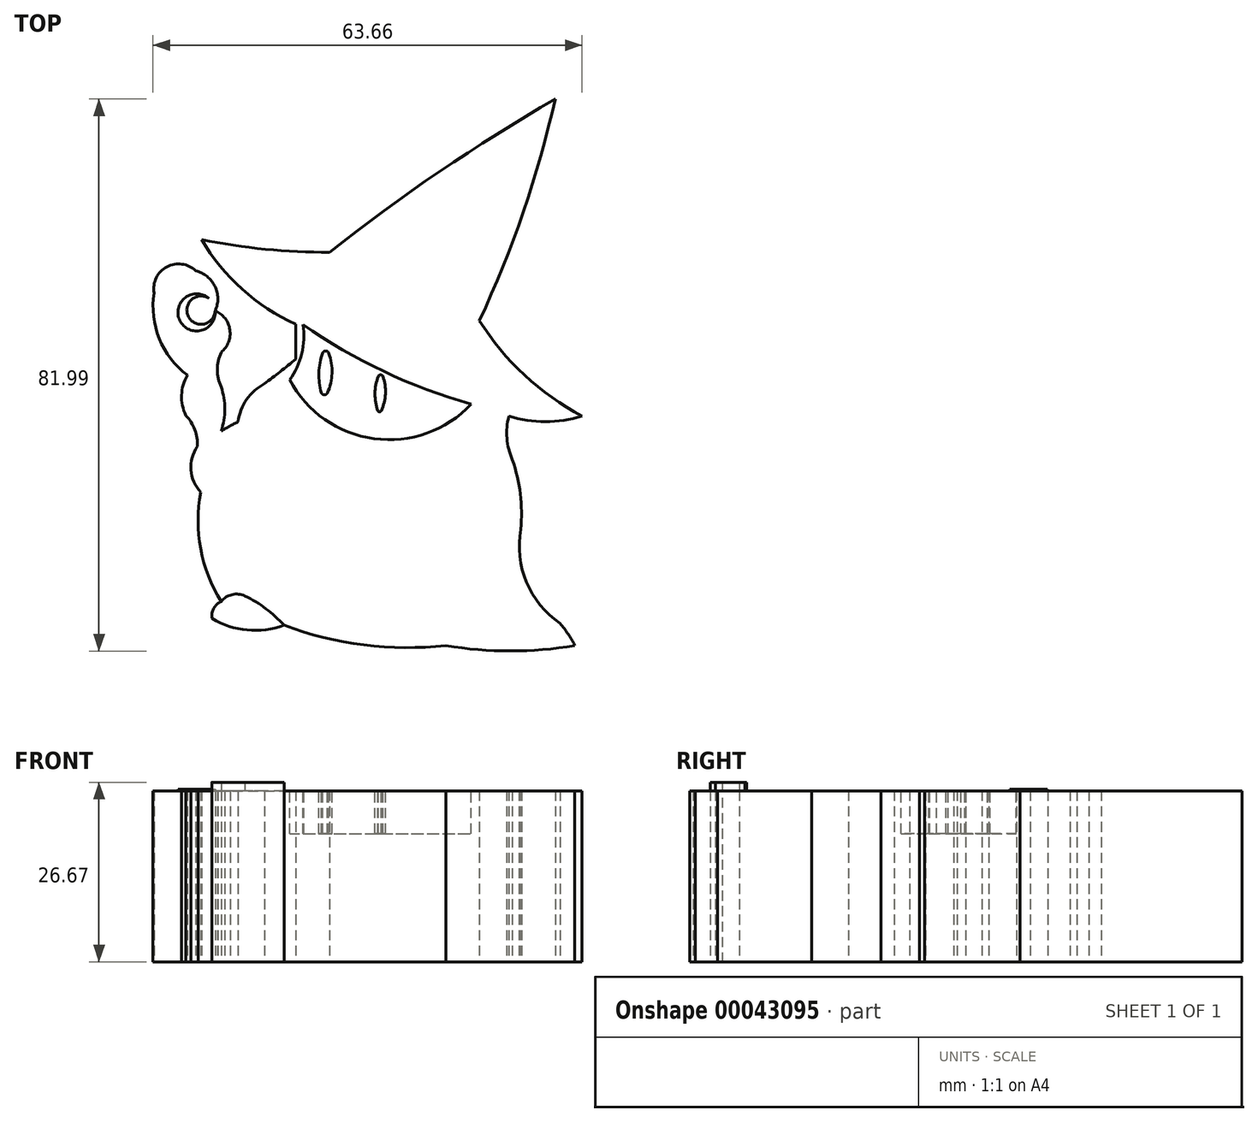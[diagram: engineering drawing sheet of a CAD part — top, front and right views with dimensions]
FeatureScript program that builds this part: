
annotation { "Feature Type Name" : "Feature", "Feature Type Description" : "" }
export const myFeature = defineFeature(function(context is Context, id is Id, definition is map)
    precondition{}
    {
        {
            var Q0;
            Q0=qCreatedBy(makeId("Top.planeOp"),FACE);
            var sketch = newSketch(context, id + "F0", { "sketchPlane" : qUnion([Q0])});
            skPoint(sketch, "E0", {"position": v(49.54, 7.17) * mm});
            skPoint(sketch, "E1", {"position": v(68.68, 7.17) * mm});
            skPoint(sketch, "E2", {"position": v(25.5, 10.19) * mm});
            skPoint(sketch, "E3", {"position": v(14.8, 11.2) * mm});
            skPoint(sketch, "E4", {"position": v(16.18, 13.71) * mm});
            skPoint(sketch, "E5", {"position": v(13.16, 29.95) * mm});
            skPoint(sketch, "E6", {"position": v(12.66, 36.75) * mm});
            skPoint(sketch, "E7", {"position": v(11.15, 47.32) * mm});
            skPoint(sketch, "E8", {"position": v(6.22, 59.55) * mm});
            skPoint(sketch, "E9", {"position": v(12.39, 62.82) * mm});
            skPoint(sketch, "E10", {"position": v(15.29, 56.9) * mm});
            skPoint(sketch, "E11", {"position": v(16.17, 50.73) * mm});
            skPoint(sketch, "E12", {"position": v(16.17, 45.57) * mm});
            skPoint(sketch, "E13", {"position": v(16.17, 39.03) * mm});
            skPoint(sketch, "E14", {"position": v(18.68, 40.41) * mm});
            skPoint(sketch, "E15", {"position": v(22.59, 46.08) * mm});
            skPoint(sketch, "E16", {"position": v(27.24, 49.73) * mm});
            skPoint(sketch, "E17", {"position": v(27.24, 54.89) * mm});
            skPoint(sketch, "E18", {"position": v(13.27, 67.48) * mm});
            skPoint(sketch, "E19", {"position": v(32.28, 65.59) * mm});
            skArc(sketch, "E20", {"start": v(49.54, 7.17) * mm, "mid": v(59.1, 6.36) * mm, "end": v(68.68, 7.17) * mm});
            skArc(sketch, "E21", {"start": v(25.5, 10.19) * mm, "mid": v(37.34, 7.27) * mm, "end": v(49.54, 7.17) * mm});
            skArc(sketch, "E22", {"start": v(14.8, 11.2) * mm, "mid": v(20.03, 9.47) * mm, "end": v(25.5, 10.19) * mm});
            skArc(sketch, "E23", {"start": v(16.18, 13.71) * mm, "mid": v(15.07, 12.69) * mm, "end": v(14.8, 11.2) * mm});
            skArc(sketch, "E24", {"start": v(13.16, 29.95) * mm, "mid": v(13.14, 21.55) * mm, "end": v(16.18, 13.71) * mm});
            skArc(sketch, "E25", {"start": v(12.66, 36.75) * mm, "mid": v(11.67, 33.26) * mm, "end": v(13.16, 29.95) * mm});
            skArc(sketch, "E26", {"start": v(12.66, 36.75) * mm, "mid": v(12.26, 39.22) * mm, "end": v(10.93, 41.34) * mm});
            skArc(sketch, "E27", {"start": v(11.15, 47.32) * mm, "mid": v(10.3, 44.36) * mm, "end": v(10.93, 41.34) * mm});
            skArc(sketch, "E28", {"start": v(6.22, 59.55) * mm, "mid": v(6.98, 52.75) * mm, "end": v(11.15, 47.32) * mm});
            skArc(sketch, "E29", {"start": v(12.39, 62.82) * mm, "mid": v(8.1, 63.44) * mm, "end": v(6.22, 59.55) * mm});
            skArc(sketch, "E30", {"start": v(15.29, 56.9) * mm, "mid": v(15.25, 60.55) * mm, "end": v(12.39, 62.82) * mm});
            skArc(sketch, "E31", {"start": v(16.17, 50.73) * mm, "mid": v(17.47, 54.07) * mm, "end": v(15.29, 56.9) * mm});
            skArc(sketch, "E32", {"start": v(16.17, 50.73) * mm, "mid": v(15.61, 48.15) * mm, "end": v(16.17, 45.57) * mm});
            skArc(sketch, "E33", {"start": v(16.17, 39.03) * mm, "mid": v(16.7, 42.3) * mm, "end": v(16.17, 45.57) * mm});
            skArc(sketch, "E34", {"start": v(18.68, 40.41) * mm, "mid": v(17.41, 39.74) * mm, "end": v(16.17, 39.03) * mm});
            skArc(sketch, "E35", {"start": v(22.59, 46.08) * mm, "mid": v(19.96, 43.71) * mm, "end": v(18.68, 40.41) * mm});
            skArc(sketch, "E36", {"start": v(22.59, 46.08) * mm, "mid": v(24.95, 47.86) * mm, "end": v(27.24, 49.73) * mm});
            skLineSegment(sketch, "E37", {"start": v(27.24, 54.89) * mm, "end": v(27.24, 49.73) * mm});
            skArc(sketch, "E38", {"start": v(13.27, 67.48) * mm, "mid": v(19.28, 60.1) * mm, "end": v(27.24, 54.89) * mm});
            skArc(sketch, "E39", {"start": v(13.27, 67.48) * mm, "mid": v(22.73, 66.05) * mm, "end": v(32.28, 65.59) * mm});
            skArc(sketch, "E40", {"start": v(65.76, 88.35) * mm, "mid": v(48.6, 77.58) * mm, "end": v(32.28, 65.59) * mm});
            skArc(sketch, "E41", {"start": v(54.5, 55.41) * mm, "mid": v(61.02, 71.58) * mm, "end": v(65.76, 88.35) * mm});
            skArc(sketch, "E42", {"start": v(54.5, 55.41) * mm, "mid": v(61.2, 47.34) * mm, "end": v(69.72, 41.24) * mm});
            skArc(sketch, "E43", {"start": v(58.88, 41.24) * mm, "mid": v(64.3, 40.44) * mm, "end": v(69.72, 41.24) * mm});
            skArc(sketch, "E44", {"start": v(58.88, 41.24) * mm, "mid": v(58.6, 37.96) * mm, "end": v(59.4, 34.77) * mm});
            skArc(sketch, "E45", {"start": v(60.65, 24.45) * mm, "mid": v(60.58, 29.68) * mm, "end": v(59.4, 34.77) * mm});
            skArc(sketch, "E46", {"start": v(60.65, 24.45) * mm, "mid": v(61.48, 16.6) * mm, "end": v(66.49, 10.49) * mm});
            skArc(sketch, "E47", {"start": v(68.68, 7.17) * mm, "mid": v(67.67, 8.88) * mm, "end": v(66.49, 10.49) * mm});
            skSolve(sketch);
        }
        {
            var Q0;
            Q0=makeQuery(id+"F0.imprint","IMPRINT",FACE,{"disambiguationData":[TD([[makeQuery(id+"F0.imprint","IMPRINT",EDGE,{"derivedFrom":sQuery(id+"F0.wireOp",EDGE,"E20")}),1.0]])]});
            extrude(context, id + "F1", {"entities" : qUnion([Q0]), "depth" : 25.4 * mm});
        }
        {
            var Q0;
            Q0=makeQuery(id+"F1.opExtrude","CAP_FACE",FACE,{"disambiguationData":[OSD([sQuery(id+"F0.wireOp",EDGE,"E20"),sQuery(id+"F0.wireOp",EDGE,"E21"),sQuery(id+"F0.wireOp",EDGE,"E22"),sQuery(id+"F0.wireOp",EDGE,"E23"),sQuery(id+"F0.wireOp",EDGE,"E24"),sQuery(id+"F0.wireOp",EDGE,"E25"),sQuery(id+"F0.wireOp",EDGE,"E26"),sQuery(id+"F0.wireOp",EDGE,"E27"),sQuery(id+"F0.wireOp",EDGE,"E28"),sQuery(id+"F0.wireOp",EDGE,"E29"),sQuery(id+"F0.wireOp",EDGE,"E30"),sQuery(id+"F0.wireOp",EDGE,"E31"),sQuery(id+"F0.wireOp",EDGE,"E32"),sQuery(id+"F0.wireOp",EDGE,"E33"),sQuery(id+"F0.wireOp",EDGE,"E34"),sQuery(id+"F0.wireOp",EDGE,"E35"),sQuery(id+"F0.wireOp",EDGE,"E36"),sQuery(id+"F0.wireOp",EDGE,"E37"),sQuery(id+"F0.wireOp",EDGE,"E38"),sQuery(id+"F0.wireOp",EDGE,"E39"),sQuery(id+"F0.wireOp",EDGE,"E40"),sQuery(id+"F0.wireOp",EDGE,"E41"),sQuery(id+"F0.wireOp",EDGE,"E42"),sQuery(id+"F0.wireOp",EDGE,"E43"),sQuery(id+"F0.wireOp",EDGE,"E44"),sQuery(id+"F0.wireOp",EDGE,"E45"),sQuery(id+"F0.wireOp",EDGE,"E46"),sQuery(id+"F0.wireOp",EDGE,"E47")])],"isStart":false});
            var sketch = newSketch(context, id + "F2", { "sketchPlane" : qUnion([Q0])});
            skArc(sketch, "E48", {"start": v(14.37, 58.73) * mm, "mid": v(10.05, 55.43) * mm, "end": v(15.29, 56.9) * mm});
            skArc(sketch, "E49", {"start": v(14.37, 58.73) * mm, "mid": v(11.3, 56.05) * mm, "end": v(15.29, 56.9) * mm});
            skSolve(sketch);
        }
        {
            var Q0;
            Q0=makeQuery(id+"F2.imprint","IMPRINT",FACE,{"disambiguationData":[TD([[makeQuery(id+"F2.imprint","IMPRINT",EDGE,{"derivedFrom":sQuery(id+"F2.wireOp",EDGE,"E48")}),1.0]])]});
            extrude(context, id + "F3", {"entities" : qUnion([Q0]), "operationType" : NewBodyOperationType.ADD, "depth" : 0.25 * mm});
        }
        {
            var Q0;
            Q0=makeQuery(id+"F1.opExtrude","CAP_FACE",FACE,{"disambiguationData":[OSD([sQuery(id+"F0.wireOp",EDGE,"E20"),sQuery(id+"F0.wireOp",EDGE,"E21"),sQuery(id+"F0.wireOp",EDGE,"E22"),sQuery(id+"F0.wireOp",EDGE,"E23"),sQuery(id+"F0.wireOp",EDGE,"E24"),sQuery(id+"F0.wireOp",EDGE,"E25"),sQuery(id+"F0.wireOp",EDGE,"E26"),sQuery(id+"F0.wireOp",EDGE,"E27"),sQuery(id+"F0.wireOp",EDGE,"E28"),sQuery(id+"F0.wireOp",EDGE,"E29"),sQuery(id+"F0.wireOp",EDGE,"E30"),sQuery(id+"F0.wireOp",EDGE,"E31"),sQuery(id+"F0.wireOp",EDGE,"E32"),sQuery(id+"F0.wireOp",EDGE,"E33"),sQuery(id+"F0.wireOp",EDGE,"E34"),sQuery(id+"F0.wireOp",EDGE,"E35"),sQuery(id+"F0.wireOp",EDGE,"E36"),sQuery(id+"F0.wireOp",EDGE,"E37"),sQuery(id+"F0.wireOp",EDGE,"E38"),sQuery(id+"F0.wireOp",EDGE,"E39"),sQuery(id+"F0.wireOp",EDGE,"E40"),sQuery(id+"F0.wireOp",EDGE,"E41"),sQuery(id+"F0.wireOp",EDGE,"E42"),sQuery(id+"F0.wireOp",EDGE,"E43"),sQuery(id+"F0.wireOp",EDGE,"E44"),sQuery(id+"F0.wireOp",EDGE,"E45"),sQuery(id+"F0.wireOp",EDGE,"E46"),sQuery(id+"F0.wireOp",EDGE,"E47")])],"isStart":false});
            var sketch = newSketch(context, id + "F4", { "sketchPlane" : qUnion([Q0])});
            skArc(sketch, "E50", {"start": v(26.34, 46.63) * mm, "mid": v(38.88, 37.9) * mm, "end": v(53.27, 43.02) * mm});
            skArc(sketch, "E51", {"start": v(28.3, 54.84) * mm, "mid": v(40.3, 47.9) * mm, "end": v(53.27, 43.02) * mm});
            skArc(sketch, "E52", {"start": v(26.34, 46.63) * mm, "mid": v(28.15, 50.53) * mm, "end": v(28.3, 54.84) * mm});
            skArc(sketch, "E53", {"start": v(31.25, 50.63) * mm, "mid": v(30.68, 47.68) * mm, "end": v(31.05, 44.7) * mm});
            skArc(sketch, "E54", {"start": v(31.95, 44.7) * mm, "mid": v(32.63, 47.63) * mm, "end": v(32.15, 50.6) * mm});
            skArc(sketch, "E55", {"start": v(32.15, 50.6) * mm, "mid": v(31.72, 50.94) * mm, "end": v(31.25, 50.63) * mm});
            skArc(sketch, "E56", {"start": v(31.05, 44.7) * mm, "mid": v(31.5, 44.42) * mm, "end": v(31.95, 44.7) * mm});
            skArc(sketch, "E57", {"start": v(39.48, 47.17) * mm, "mid": v(39.01, 44.6) * mm, "end": v(39.44, 42) * mm});
            skArc(sketch, "E58", {"start": v(39.92, 42.02) * mm, "mid": v(40.56, 44.57) * mm, "end": v(40.18, 47.17) * mm});
            skArc(sketch, "E59", {"start": v(40.18, 47.17) * mm, "mid": v(39.83, 47.38) * mm, "end": v(39.48, 47.17) * mm});
            skArc(sketch, "E60", {"start": v(39.44, 42) * mm, "mid": v(39.68, 41.89) * mm, "end": v(39.92, 42.02) * mm});
            skSolve(sketch);
        }
        {
            var Q0;
            Q0 = qSketchRegion(id + "F4", true);
            extrude(context, id + "F5", {"entities" : qUnion([Q0]), "operationType" : NewBodyOperationType.REMOVE, "oppositeDirection" : true, "depth" : 6.35 * mm});
        }
        {
            var Q0;
            {var subQ0=sQuery(id+"F0.wireOp",EDGE,"E20");var subQ1=sQuery(id+"F0.wireOp",EDGE,"E21");var subQ2=sQuery(id+"F0.wireOp",EDGE,"E22");var subQ3=sQuery(id+"F0.wireOp",EDGE,"E23");var subQ4=sQuery(id+"F0.wireOp",EDGE,"E24");var subQ5=sQuery(id+"F0.wireOp",EDGE,"E25");var subQ6=sQuery(id+"F0.wireOp",EDGE,"E26");var subQ7=sQuery(id+"F0.wireOp",EDGE,"E27");var subQ8=sQuery(id+"F0.wireOp",EDGE,"E28");var subQ9=sQuery(id+"F0.wireOp",EDGE,"E29");var subQ10=sQuery(id+"F0.wireOp",EDGE,"E30");var subQ11=sQuery(id+"F0.wireOp",EDGE,"E31");var subQ12=sQuery(id+"F0.wireOp",EDGE,"E32");var subQ13=sQuery(id+"F0.wireOp",EDGE,"E33");var subQ14=sQuery(id+"F0.wireOp",EDGE,"E34");var subQ15=sQuery(id+"F0.wireOp",EDGE,"E35");var subQ16=sQuery(id+"F0.wireOp",EDGE,"E36");var subQ17=sQuery(id+"F0.wireOp",EDGE,"E37");var subQ18=sQuery(id+"F0.wireOp",EDGE,"E38");var subQ19=sQuery(id+"F0.wireOp",EDGE,"E39");var subQ20=sQuery(id+"F0.wireOp",EDGE,"E40");var subQ21=sQuery(id+"F0.wireOp",EDGE,"E41");var subQ22=sQuery(id+"F0.wireOp",EDGE,"E42");var subQ23=sQuery(id+"F0.wireOp",EDGE,"E43");var subQ24=sQuery(id+"F0.wireOp",EDGE,"E44");var subQ25=sQuery(id+"F0.wireOp",EDGE,"E45");var subQ26=sQuery(id+"F0.wireOp",EDGE,"E46");var subQ27=sQuery(id+"F0.wireOp",EDGE,"E47");Q0=makeQuery(id+"F5.boolean.opBoolean","SPLIT",FACE,{"disambiguationData":[TD([makeQuery(id+"F1.opExtrude","SWEPT_FACE",FACE,{"disambiguationData":[OSD([subQ0])]})])],"derivedFrom":makeQuery(id+"F1.opExtrude","CAP_FACE",FACE,{"disambiguationData":[OSD([subQ0,subQ1,subQ2,subQ3,subQ4,subQ5,subQ6,subQ7,subQ8,subQ9,subQ10,subQ11,subQ12,subQ13,subQ14,subQ15,subQ16,subQ17,subQ18,subQ19,subQ20,subQ21,subQ22,subQ23,subQ24,subQ25,subQ26,subQ27])],"isStart":false})});}
            var sketch = newSketch(context, id + "F6", { "sketchPlane" : qUnion([Q0])});
            skPoint(sketch, "E61", {"position": v(16.64, 10.29) * mm});
            skPoint(sketch, "E62", {"position": v(15.07, 12.69) * mm});
            skArc(sketch, "E63", {"start": v(16.18, 13.71) * mm, "mid": v(15.07, 12.69) * mm, "end": v(14.8, 11.2) * mm});
            skArc(sketch, "E64", {"start": v(14.8, 11.2) * mm, "mid": v(20.03, 9.47) * mm, "end": v(25.5, 10.19) * mm});
            skArc(sketch, "E65", {"start": v(25.5, 10.19) * mm, "mid": v(22.81, 12.64) * mm, "end": v(19.7, 14.54) * mm});
            skArc(sketch, "E66", {"start": v(19.7, 14.54) * mm, "mid": v(17.8, 14.74) * mm, "end": v(16.18, 13.71) * mm});
            skSolve(sketch);
        }
        {
            var Q0;
            Q0 = qSketchRegion(id + "F6", true);
            extrude(context, id + "F7", {"entities" : qUnion([Q0]), "operationType" : NewBodyOperationType.ADD, "depth" : 1.27 * mm});
        }
    });
